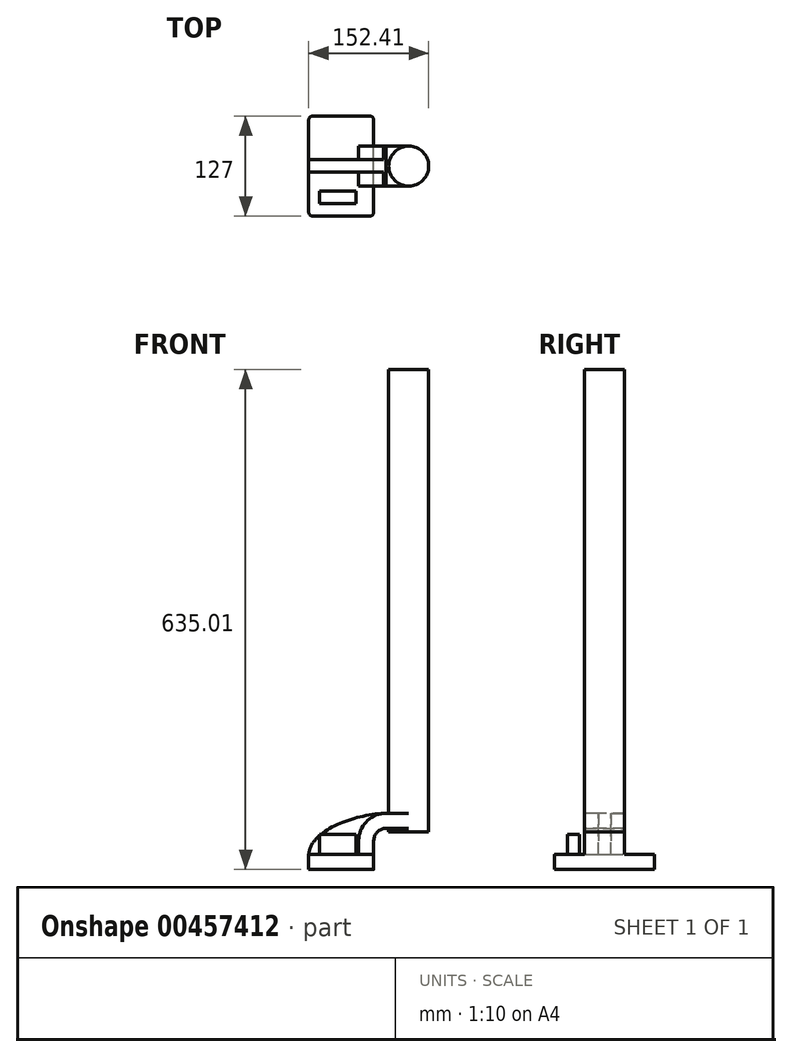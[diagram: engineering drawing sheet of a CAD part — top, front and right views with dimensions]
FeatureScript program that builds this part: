
annotation { "Feature Type Name" : "Feature", "Feature Type Description" : "" }
export const myFeature = defineFeature(function(context is Context, id is Id, definition is map)
    precondition{}
    {
        {
            var Q0;
            Q0=qCreatedBy(makeId("Front.planeOp"),FACE);
            var sketch = newSketch(context, id + "F0", { "sketchPlane" : qUnion([Q0])});
            skLineSegment(sketch, "E0.rect.bottom", {"start": v(-41.28, 9.52) * mm, "end": v(41.28, 9.52) * mm});
            skLineSegment(sketch, "E0.rect.top", {"start": v(-41.28, -9.52) * mm, "end": v(41.28, -9.52) * mm});
            skLineSegment(sketch, "E0.rect.left", {"start": v(-41.28, 9.52) * mm, "end": v(-41.28, -9.52) * mm});
            skLineSegment(sketch, "E0.rect.right", {"start": v(41.28, 9.52) * mm, "end": v(41.28, -9.52) * mm});
            skPoint(sketch, "E0.rect.middle", {"position": v(0, 0) * mm});
            skLineSegment(sketch, "E1", {"start": v(41.28, 9.52) * mm, "end": v(41.28, 27) * mm});
            skArc(sketch, "E2", {"start": v(41.28, 27) * mm, "mid": v(45.92, 38.23) * mm, "end": v(57.15, 42.88) * mm});
            skLineSegment(sketch, "E3", {"start": v(57.15, 42.88) * mm, "end": v(85.72, 42.88) * mm});
            skLineSegment(sketch, "E4.rect.bottom", {"start": v(60.32, 38.1) * mm, "end": v(111.12, 38.1) * mm});
            skLineSegment(sketch, "E4.rect.top", {"start": v(60.32, 66.68) * mm, "end": v(111.12, 66.68) * mm});
            skLineSegment(sketch, "E4.rect.left", {"start": v(60.32, 38.1) * mm, "end": v(60.32, 66.68) * mm});
            skLineSegment(sketch, "E4.rect.right", {"start": v(111.13, 38.1) * mm, "end": v(111.12, 66.68) * mm});
            skPoint(sketch, "E4.rect.middle", {"position": v(85.72, 52.39) * mm});
            skLineSegment(sketch, "E5.0", {"start": v(57.15, 61.93) * mm, "end": v(85.72, 61.93) * mm});
            skArc(sketch, "E5.1", {"start": v(22.23, 27) * mm, "mid": v(32.45, 51.7) * mm, "end": v(57.15, 61.93) * mm});
            skLineSegment(sketch, "E5.2", {"start": v(22.23, 9.52) * mm, "end": v(22.23, 27) * mm});
            skLineSegment(sketch, "E6", {"start": v(85.72, 38.1) * mm, "end": v(85.72, 66.68) * mm});
            skFitSpline(sketch, "E7", {"points": [v(-41.28, 9.53) * mm, v(57.15, 61.93) * mm], "startDerivative": vector(5.2, 92.34) * mm, "endDerivative": vector(120.92, 4.22) * mm});
            skSolve(sketch);
        }
        {
            var Q0;
            Q0=makeQuery(id+"F0.imprint","IMPRINT",FACE,{"disambiguationData":[TD([[makeQuery(id+"F0.imprint","IMPRINT",EDGE,{"derivedFrom":sQuery(id+"F0.wireOp",EDGE,"E0.rect.top")}),1.0]])]});
            extrude(context, id + "F1", {"entities" : qUnion([Q0]), "endBound" : BoundingType.SYMMETRIC, "depth" : 127 * mm});
        }
        {
            var Q0;
            {var subQ9=sQuery(id+"F0.wireOp",EDGE,"E1");Q0=makeQuery(id+"F0.imprint","IMPRINT",FACE,{"disambiguationData":[TD([[makeQuery(id+"F0.imprint","IMPRINT",EDGE,{"derivedFrom":subQ9}),1.0]])]});}
            var Q1;
            {var subQ0=sQuery(id+"F0.wireOp",EDGE,"E6");var subQ1=sQuery(id+"F0.wireOp",EDGE,"E3");var subQ2=makeQuery(id+"F0.imprint","INTERSECT",VERTEX,{"derivedFrom":[subQ1,subQ0]});Q1=makeQuery(id+"F0.imprint","IMPRINT",FACE,{"disambiguationData":[TD([[makeQuery(id+"F0.imprint","IMPRINT",EDGE,{"disambiguationData":[TD([[subQ2,1.0]])],"derivedFrom":subQ1}),1.0]])]});}
            extrude(context, id + "F2", {"entities" : qUnion([Q0, Q1]), "operationType" : NewBodyOperationType.ADD, "endBound" : BoundingType.SYMMETRIC, "depth" : 50.8 * mm});
        }
        {
            var Q0;
            {var subQ3=sQuery(id+"F0.wireOp",EDGE,"E5.2");Q0=makeQuery(id+"F0.imprint","IMPRINT",FACE,{"disambiguationData":[TD([[makeQuery(id+"F0.imprint","IMPRINT",EDGE,{"derivedFrom":subQ3}),1.0]])]});}
            extrude(context, id + "F3", {"entities" : qUnion([Q0]), "operationType" : NewBodyOperationType.ADD, "endBound" : BoundingType.SYMMETRIC, "depth" : 15.88 * mm});
        }
        {
            var Q0;
            {var subQ5=sQuery(id+"F0.wireOp",EDGE,"E4.rect.right");Q0=makeQuery(id+"F0.imprint","IMPRINT",FACE,{"disambiguationData":[TD([[makeQuery(id+"F0.imprint","IMPRINT",EDGE,{"derivedFrom":subQ5}),1.0]])]});}
            var Q1;
            Q1=sQuery(id+"F0.wireOp",EDGE,"E6");
            revolve(context, id + "F4", {"operationType" : NewBodyOperationType.ADD, "entities" : qUnion([Q0]), "axis" : qUnion([Q1]), "revolveType" : RevolveType.FULL});
        }
        {
            var Q0;
            Q0=makeQuery(id+"F1.opExtrude","CAP_EDGE",EDGE,{"disambiguationData":[OSD([sQuery(id+"F0.wireOp",EDGE,"E0.rect.right")])],"isStart":false});
            var Q1;
            Q1=makeQuery(id+"F1.opExtrude","CAP_EDGE",EDGE,{"disambiguationData":[OSD([sQuery(id+"F0.wireOp",EDGE,"E0.rect.left")])],"isStart":false});
            var Q2;
            Q2=makeQuery(id+"F1.opExtrude","CAP_EDGE",EDGE,{"disambiguationData":[OSD([sQuery(id+"F0.wireOp",EDGE,"E0.rect.right")])],"isStart":true});
            var Q3;
            Q3=makeQuery(id+"F1.opExtrude","CAP_EDGE",EDGE,{"disambiguationData":[OSD([sQuery(id+"F0.wireOp",EDGE,"E0.rect.left")])],"isStart":true});
            fillet(context, id + "F5", {"entities" : qUnion([Q0, Q1, Q2, Q3]), "radius" : 5.08 * mm, "tangentPropagation" : true, "allowEdgeOverflow" : false});
        }
        {
            var Q0;
            Q0=makeQuery(id+"F4.opRevolve","SWEPT_FACE",FACE,{"disambiguationData":[OSD([sQuery(id+"F0.wireOp",EDGE,"E4.rect.top")])]});
            var sketch = newSketch(context, id + "F6", { "sketchPlane" : qUnion([Q0])});
            skSolve(sketch);
        }
        {
            var Q0;
            Q0=makeQuery(id+"F6.imprint","IMPRINT",FACE,{"disambiguationData":[TD([[makeQuery(id+"F6.imprint","IMPRINT",EDGE,{"derivedFrom":makeQuery(id+"F4.opRevolve","SWEPT_EDGE",EDGE,{"disambiguationData":[OSD([sQuery(id+"F0.wireOp",EDGE,"E4.rect.top"),sQuery(id+"F0.wireOp",EDGE,"E4.rect.right")])]})}),-1.0]])]});
            extrude(context, id + "F7", {"entities" : qUnion([Q0]), "operationType" : NewBodyOperationType.ADD, "depth" : 558.8 * mm});
        }
        {
            var Q0;
            {var subQ4=sQuery(id+"F0.wireOp",EDGE,"E0.rect.bottom");var subQ5=sQuery(id+"F0.wireOp",EDGE,"E0.rect.right");var subQ6=sQuery(id+"F0.wireOp",EDGE,"E0.rect.left");Q0=makeQuery(id+"F3.boolean.opBoolean","SPLIT",FACE,{"disambiguationData":[TD([makeQuery(id+"F1.opExtrude","CAP_FACE",FACE,{"disambiguationData":[OSD([subQ4,sQuery(id+"F0.wireOp",EDGE,"E0.rect.top"),subQ6,subQ5])],"isStart":false})])],"derivedFrom":makeQuery(id+"F1.opExtrude","SWEPT_FACE",FACE,{"disambiguationData":[OSD([subQ4])]})});}
            var sketch = newSketch(context, id + "F8", { "sketchPlane" : qUnion([Q0])});
            skLineSegment(sketch, "E8.bottom", {"start": v(19.05, -47.5) * mm, "end": v(-27.48, -47.5) * mm});
            skLineSegment(sketch, "E8.top", {"start": v(19.05, -31.9) * mm, "end": v(-27.48, -31.9) * mm});
            skLineSegment(sketch, "E8.left", {"start": v(19.05, -47.5) * mm, "end": v(19.05, -31.9) * mm});
            skLineSegment(sketch, "E8.right", {"start": v(-27.48, -47.5) * mm, "end": v(-27.48, -31.9) * mm});
            skSolve(sketch);
        }
        {
            var Q0;
            Q0=makeQuery(id+"F8.imprint","IMPRINT",FACE,{"disambiguationData":[TD([[makeQuery(id+"F8.imprint","IMPRINT",EDGE,{"derivedFrom":sQuery(id+"F8.wireOp",EDGE,"E8.bottom")}),-1.0]])]});
            extrude(context, id + "F9", {"entities" : qUnion([Q0]), "operationType" : NewBodyOperationType.ADD, "depth" : 25.4 * mm});
        }
    });
